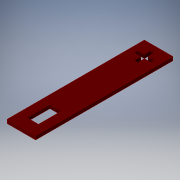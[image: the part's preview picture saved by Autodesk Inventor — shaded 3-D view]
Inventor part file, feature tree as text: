
AUTODESK INVENTOR PART (.ipt)
format: ipt  version: 2019 (Build 230136000, 136)  size: 140,800 bytes
history: native  units: mm
features: extrude x1, sketch x1
ambient origin geometry x8: Origin, YZ Plane, XZ Plane, XY Plane, X Axis, Y Axis, Z Axis, Center Point
bodies: Solid1 (feature_tree)
feature tree (2):
  extrude  "Extrusion1"  Depth=10.0mm
  sketch  "Sketch1"  dims[d8=15.0mm d9=3.18mm d10=3.18mm d11=15.0mm d12=7.5mm d13=1.59mm d16=15.0mm d18=3.18mm d19=15.0mm d20=7.5mm d21=1.59mm d24=10.0mm d25=20.0mm d26=25.0mm d27=120.0mm d28=20.0mm d29=12.5mm d30=12.5mm d31=12.5mm d32=3.18mm d33=3.18mm d34=0.0mm]
